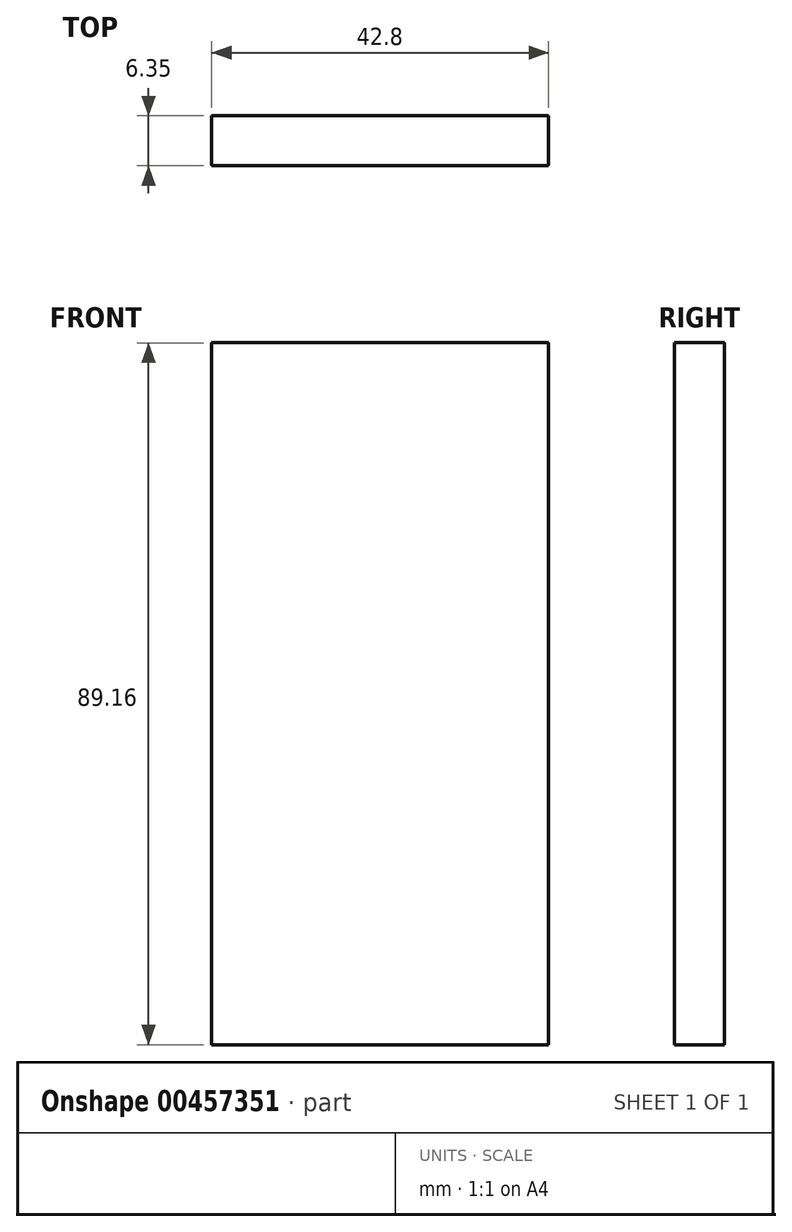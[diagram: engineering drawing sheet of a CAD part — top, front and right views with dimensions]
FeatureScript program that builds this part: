
annotation { "Feature Type Name" : "Feature", "Feature Type Description" : "" }
export const myFeature = defineFeature(function(context is Context, id is Id, definition is map)
    precondition{}
    {
        {
            var Q0;
            Q0=qCreatedBy(makeId("Front.planeOp"),FACE);
            var sketch = newSketch(context, id + "F0", { "sketchPlane" : qUnion([Q0])});
            skLineSegment(sketch, "E0.bottom", {"start": v(21.4, -44.58) * mm, "end": v(-21.4, -44.58) * mm});
            skLineSegment(sketch, "E0.top", {"start": v(21.4, 44.58) * mm, "end": v(-21.4, 44.58) * mm});
            skLineSegment(sketch, "E0.left", {"start": v(21.4, -44.58) * mm, "end": v(21.4, 44.58) * mm});
            skLineSegment(sketch, "E0.right", {"start": v(-21.4, -44.58) * mm, "end": v(-21.4, 44.58) * mm});
            skPoint(sketch, "E0.middle", {"position": v(0, 0) * mm});
            skSolve(sketch);
        }
        {
            var Q0;
            Q0 = qSketchRegion(id + "F0", true);
            extrude(context, id + "F1", {"entities" : qUnion([Q0]), "depth" : 6.35 * mm});
        }
    });
